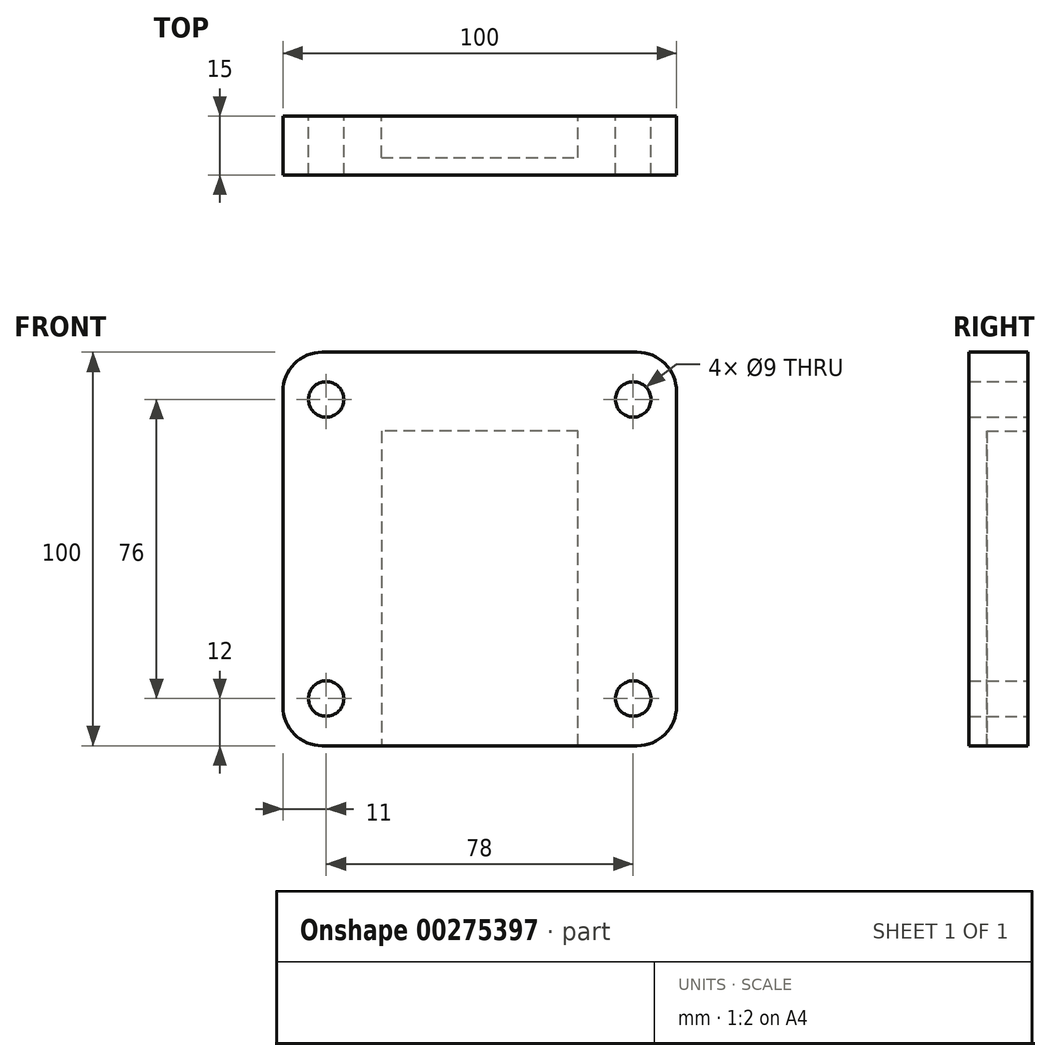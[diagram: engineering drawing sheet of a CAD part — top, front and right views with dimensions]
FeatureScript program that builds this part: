
annotation { "Feature Type Name" : "Feature", "Feature Type Description" : "" }
export const myFeature = defineFeature(function(context is Context, id is Id, definition is map)
    precondition{}
    {
        {
            var Q0;
            Q0=qCreatedBy(makeId("Front.planeOp"),FACE);
            var sketch = newSketch(context, id + "F0", { "sketchPlane" : qUnion([Q0])});
            skLineSegment(sketch, "E0.bottom", {"start": v(-40, 50) * mm, "end": v(40, 50) * mm});
            skLineSegment(sketch, "E0.top", {"start": v(-40, -50) * mm, "end": v(40, -50) * mm});
            skLineSegment(sketch, "E0.left", {"start": v(-50, 40) * mm, "end": v(-50, -40) * mm});
            skLineSegment(sketch, "E0.right", {"start": v(50, 40) * mm, "end": v(50, -40) * mm});
            skPoint(sketch, "E1.visualSharp", {"position": v(-50, 50) * mm});
            skArc(sketch, "E1.filletArc", {"start": v(-40, 50) * mm, "mid": v(-47.07, 47.07) * mm, "end": v(-50, 40) * mm});
            skPoint(sketch, "E2.visualSharp", {"position": v(50, 50) * mm});
            skArc(sketch, "E2.filletArc", {"start": v(50, 40) * mm, "mid": v(47.07, 47.07) * mm, "end": v(40, 50) * mm});
            skPoint(sketch, "E3.visualSharp", {"position": v(50, -50) * mm});
            skArc(sketch, "E3.filletArc", {"start": v(40, -50) * mm, "mid": v(47.07, -47.07) * mm, "end": v(50, -40) * mm});
            skPoint(sketch, "E4.visualSharp", {"position": v(-50, -50) * mm});
            skArc(sketch, "E4.filletArc", {"start": v(-50, -40) * mm, "mid": v(-47.07, -47.07) * mm, "end": v(-40, -50) * mm});
            skCircle(sketch, "E5", {"center": v(-39, 38) * mm, "radius": 4.5 * mm});
            skCircle(sketch, "E6", {"center": v(39, 38) * mm, "radius": 4.5 * mm});
            skCircle(sketch, "E7", {"center": v(39, -38) * mm, "radius": 4.5 * mm});
            skCircle(sketch, "E8", {"center": v(-39, -38) * mm, "radius": 4.5 * mm});
            skSolve(sketch);
        }
        {
            var Q0;
            Q0=makeQuery(id+"F0.imprint","IMPRINT",FACE,{"disambiguationData":[TD([[makeQuery(id+"F0.imprint","IMPRINT",EDGE,{"derivedFrom":sQuery(id+"F0.wireOp",EDGE,"E0.bottom")}),-1.0]])]});
            extrude(context, id + "F1", {"entities" : qUnion([Q0]), "depth" : 15 * mm});
        }
        {
            var Q0;
            Q0=makeQuery(id+"F1.opExtrude","CAP_FACE",FACE,{"disambiguationData":[OSD([sQuery(id+"F0.wireOp",EDGE,"E0.bottom"),sQuery(id+"F0.wireOp",EDGE,"E0.top"),sQuery(id+"F0.wireOp",EDGE,"E0.left"),sQuery(id+"F0.wireOp",EDGE,"E0.right"),sQuery(id+"F0.wireOp",EDGE,"E1.filletArc"),sQuery(id+"F0.wireOp",EDGE,"E2.filletArc"),sQuery(id+"F0.wireOp",EDGE,"E3.filletArc"),sQuery(id+"F0.wireOp",EDGE,"E4.filletArc")])],"isStart":true});
            var sketch = newSketch(context, id + "F2", { "sketchPlane" : qUnion([Q0])});
            skLineSegment(sketch, "E9.top", {"start": v(-40.4, -50.06) * mm, "end": v(39.6, -50.06) * mm});
            skLineSegment(sketch, "E10.left", {"start": v(-25, 14.75) * mm, "end": v(-25, -50.06) * mm});
            skLineSegment(sketch, "E11.left", {"start": v(25, 29.94) * mm, "end": v(25, -50.06) * mm});
            skLineSegment(sketch, "E12", {"start": v(-25, 14.75) * mm, "end": v(-25, 30) * mm});
            skLineSegment(sketch, "E13", {"start": v(-25, 30) * mm, "end": v(25, 29.94) * mm});
            skSolve(sketch);
        }
        {
            var Q0;
            {var subQ0=sQuery(id+"F2.wireOp",EDGE,"E12");Q0=makeQuery(id+"F2.imprint","IMPRINT",FACE,{"disambiguationData":[TD([[makeQuery(id+"F2.imprint","IMPRINT",EDGE,{"derivedFrom":subQ0}),-1.0]])]});}
            extrude(context, id + "F3", {"entities" : qUnion([Q0]), "operationType" : NewBodyOperationType.REMOVE, "oppositeDirection" : true, "depth" : 10.5 * mm, "offsetDistance" : 25 * mm});
        }
    });
